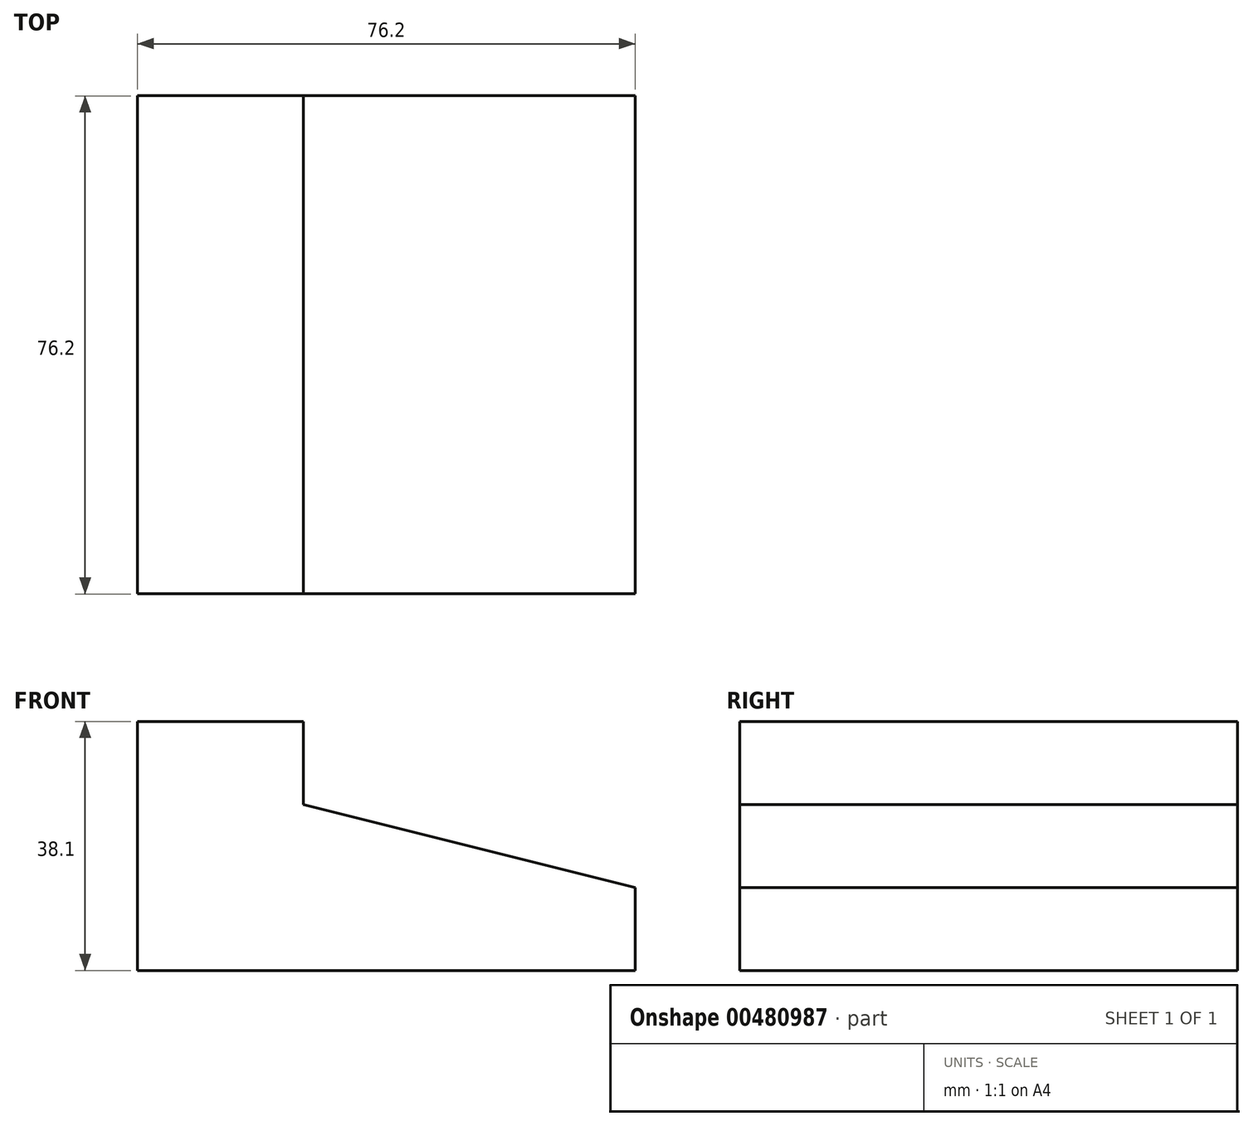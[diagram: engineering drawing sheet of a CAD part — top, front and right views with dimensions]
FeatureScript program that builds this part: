
annotation { "Feature Type Name" : "Feature", "Feature Type Description" : "" }
export const myFeature = defineFeature(function(context is Context, id is Id, definition is map)
    precondition{}
    {
        {
            var Q0;
            Q0=qCreatedBy(makeId("Top.planeOp"),FACE);
            var sketch = newSketch(context, id + "F0", { "sketchPlane" : qUnion([Q0])});
            skLineSegment(sketch, "E0.bottom", {"start": v(-37.5, -32.59) * mm, "end": v(38.7, -32.59) * mm});
            skLineSegment(sketch, "E0.top", {"start": v(-37.5, 43.61) * mm, "end": v(38.7, 43.61) * mm});
            skLineSegment(sketch, "E0.left", {"start": v(-37.5, -32.59) * mm, "end": v(-37.5, 43.61) * mm});
            skLineSegment(sketch, "E0.right", {"start": v(38.7, -32.59) * mm, "end": v(38.7, 43.61) * mm});
            skSolve(sketch);
        }
        {
            var Q0;
            Q0 = qSketchRegion(id + "F0", true);
            extrude(context, id + "F1", {"entities" : qUnion([Q0]), "depth" : 38.1 * mm});
        }
        {
            var Q0;
            Q0=makeQuery(id+"F1.opExtrude","SWEPT_FACE",FACE,{"disambiguationData":[OSD([sQuery(id+"F0.wireOp",EDGE,"E0.bottom")])]});
            var sketch = newSketch(context, id + "F2", { "sketchPlane" : qUnion([Q0])});
            skLineSegment(sketch, "E1", {"start": v(-37.5, 38.1) * mm, "end": v(-12.1, 38.1) * mm});
            skLineSegment(sketch, "E2", {"start": v(-12.1, 38.1) * mm, "end": v(-12.1, 25.4) * mm});
            skLineSegment(sketch, "E3", {"start": v(-12.1, 25.4) * mm, "end": v(38.7, 12.7) * mm});
            skLineSegment(sketch, "E4", {"start": v(38.7, 12.7) * mm, "end": v(38.7, 0) * mm});
            skSolve(sketch);
        }
        {
            var Q0;
            {var subQ0=sQuery(id+"F2.wireOp",EDGE,"E2");Q0=makeQuery(id+"F2.imprint","IMPRINT",FACE,{"disambiguationData":[TD([[makeQuery(id+"F2.imprint","IMPRINT",EDGE,{"derivedFrom":subQ0}),1.0]])]});}
            extrude(context, id + "F3", {"entities" : qUnion([Q0]), "operationType" : NewBodyOperationType.REMOVE, "endBound" : BoundingType.THROUGH_ALL, "oppositeDirection" : true, "depth" : 25.4 * mm});
        }
    });
